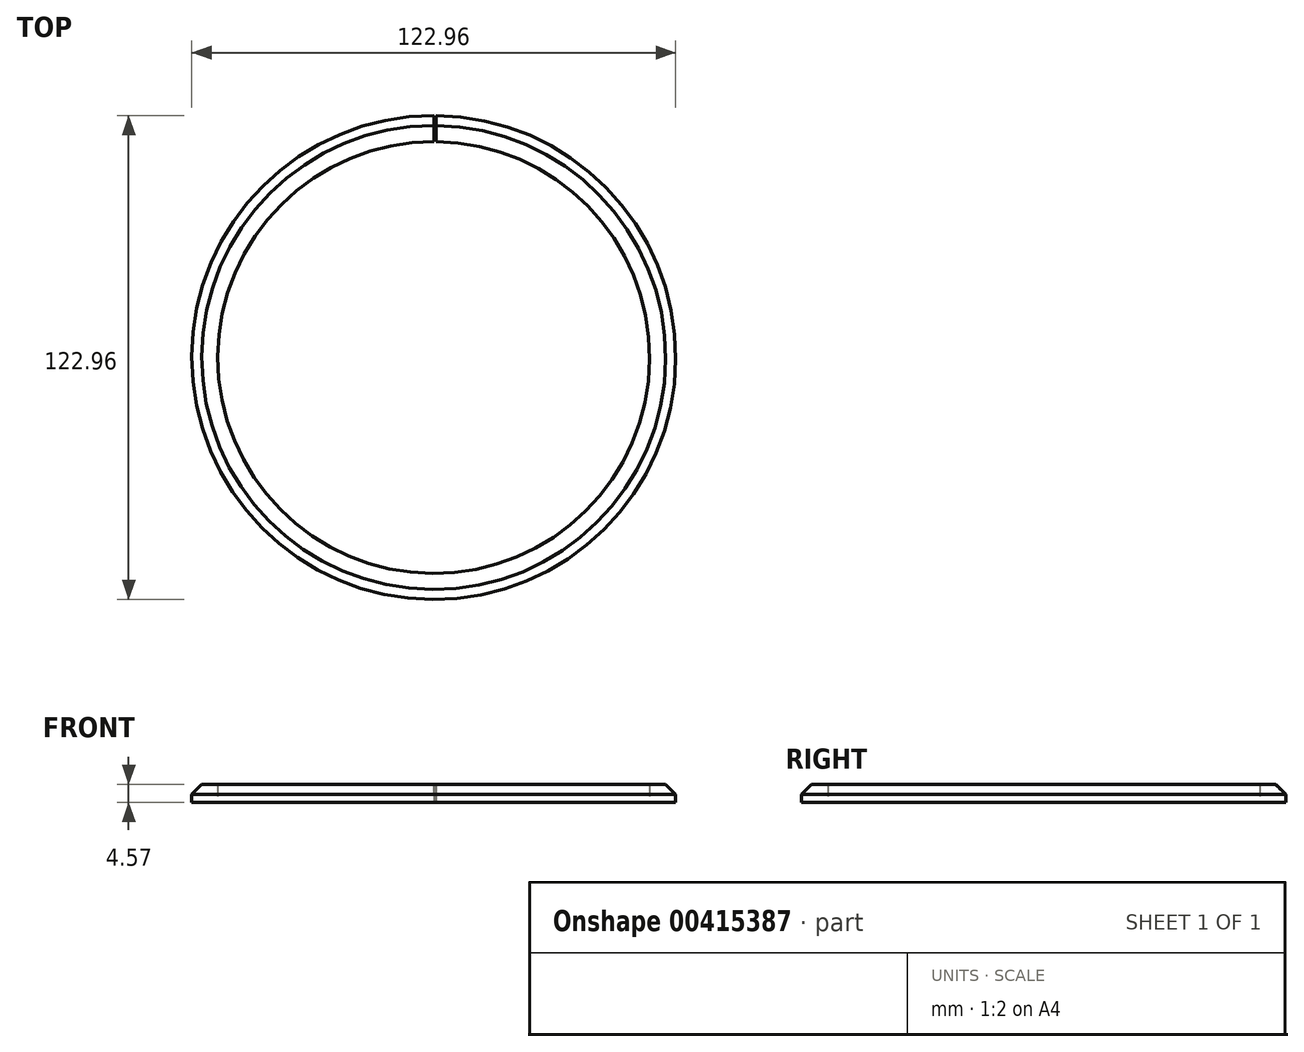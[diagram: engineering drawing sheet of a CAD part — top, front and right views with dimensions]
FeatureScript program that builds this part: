
annotation { "Feature Type Name" : "Feature", "Feature Type Description" : "" }
export const myFeature = defineFeature(function(context is Context, id is Id, definition is map)
    precondition{}
    {
        {
            var Q0;
            Q0=qCreatedBy(makeId("Top.planeOp"),FACE);
            var sketch = newSketch(context, id + "F0", { "sketchPlane" : qUnion([Q0])});
            skPoint(sketch, "E0.start.orphan", {"position": v(0, -57.12) * mm});
            skArc(sketch, "E1", {"start": v(0.05, 54.86) * mm, "mid": v(-0.3, -54.86) * mm, "end": v(0.56, 54.86) * mm});
            skArc(sketch, "E2", {"start": v(0.05, 61.48) * mm, "mid": v(-0.3, -61.48) * mm, "end": v(0.56, 61.47) * mm});
            skLineSegment(sketch, "E3", {"start": v(0.05, 61.48) * mm, "end": v(0.05, 54.86) * mm});
            skLineSegment(sketch, "E4", {"start": v(0.56, 61.47) * mm, "end": v(0.56, 54.86) * mm});
            skSolve(sketch);
        }
        {
            var Q0;
            Q0 = qSketchRegion(id + "F0", true);
            extrude(context, id + "F1", {"entities" : qUnion([Q0]), "depth" : 4.57 * mm});
        }
        {
            var Q0;
            Q0=makeQuery(id+"F1.opExtrude","CAP_EDGE",EDGE,{"disambiguationData":[OSD([sQuery(id+"F0.wireOp",EDGE,"E2")])],"isStart":false});
            chamfer(context, id + "F2", {"entities" : qUnion([Q0]), "width" : 2.54 * mm, "tangentPropagation" : true});
        }
    });
